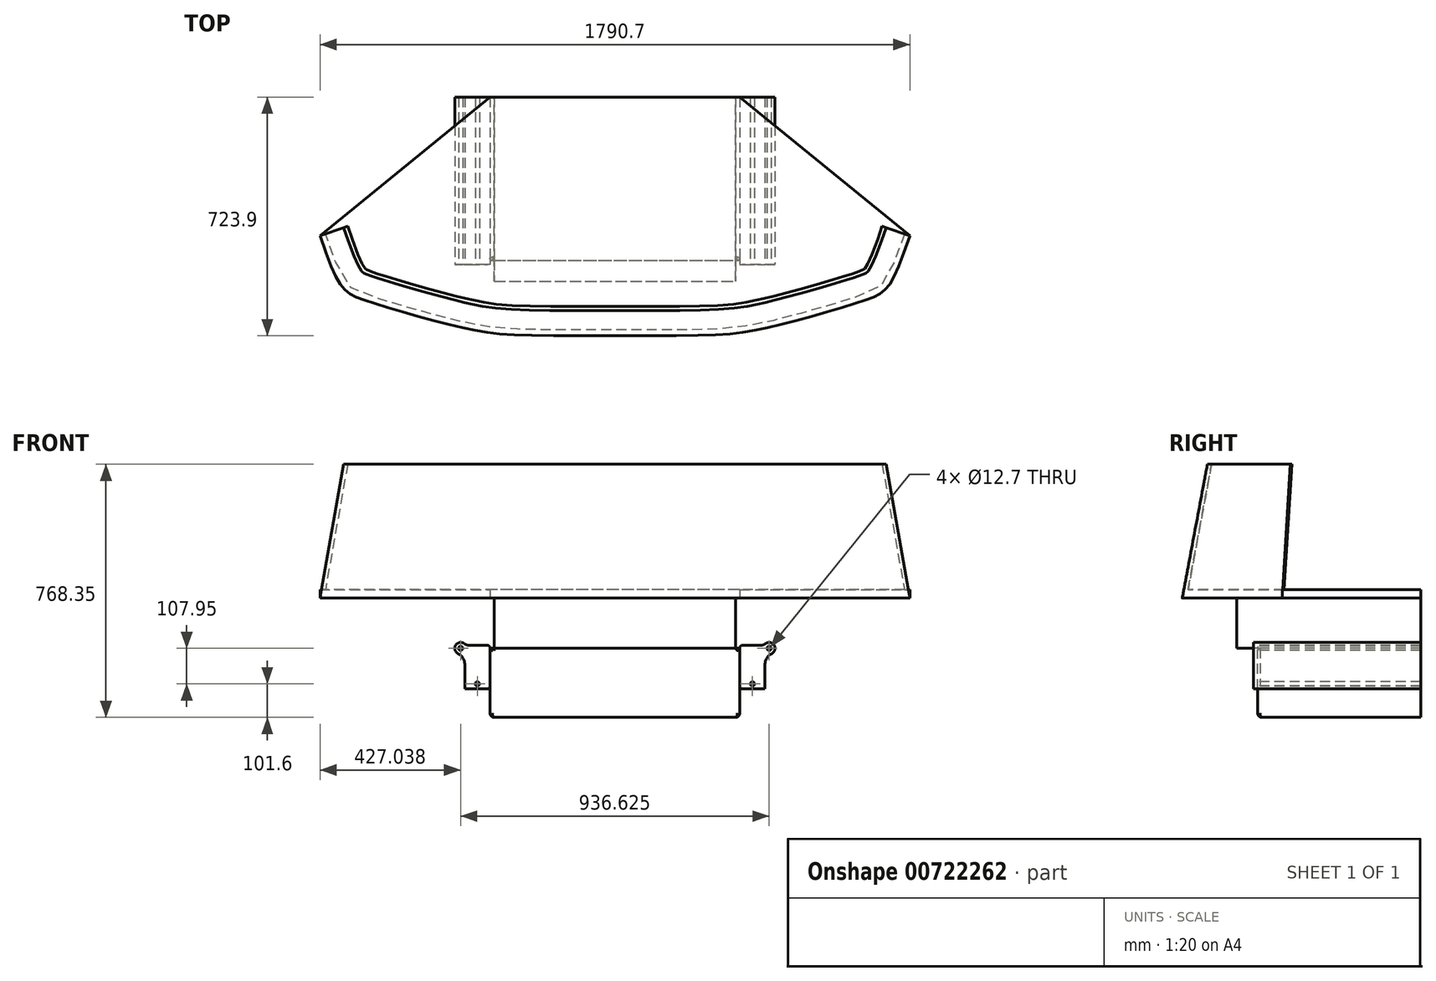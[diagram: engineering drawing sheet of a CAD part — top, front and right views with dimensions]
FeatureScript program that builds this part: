
annotation { "Feature Type Name" : "Feature", "Feature Type Description" : "" }
export const myFeature = defineFeature(function(context is Context, id is Id, definition is map)
    precondition{}
    {
        {
            var Q0;
            Q0=qCreatedBy(makeId("Front.planeOp"),FACE);
            var sketch = newSketch(context, id + "F0", { "sketchPlane" : qUnion([Q0])});
            skCircle(sketch, "E0", {"center": v(-468.31, 0) * mm, "radius": 6.35 * mm});
            skCircle(sketch, "E1", {"center": v(-417.51, -107.95) * mm, "radius": 6.35 * mm});
            skArc(sketch, "E2", {"start": v(-457.5, 14.12) * mm, "mid": v(-483.35, 9.48) * mm, "end": v(-476.4, -15.84) * mm});
            skLineSegment(sketch, "E3", {"start": v(-442.07, 8.9) * mm, "end": v(-379.41, 8.9) * mm});
            skLineSegment(sketch, "E4", {"start": v(-379.41, 8.89) * mm, "end": v(-379.41, -123.2) * mm});
            skLineSegment(sketch, "E5", {"start": v(-379.41, -123.2) * mm, "end": v(-455.61, -123.2) * mm});
            skLineSegment(sketch, "E6", {"start": v(-455.61, -123.2) * mm, "end": v(-455.61, -49.77) * mm});
            skPoint(sketch, "E7.visualSharp", {"position": v(-452.91, 8.9) * mm});
            skArc(sketch, "E7.filletArc", {"start": v(-457.5, 14.12) * mm, "mid": v(-450.22, 10.23) * mm, "end": v(-442.07, 8.89) * mm});
            skPoint(sketch, "E8.visualSharp", {"position": v(-455.61, -12.44) * mm});
            skArc(sketch, "E8.filletArc", {"start": v(-455.61, -49.77) * mm, "mid": v(-461.22, -29.88) * mm, "end": v(-476.4, -15.84) * mm});
            skLineSegment(sketch, "E9.MirrorCS", {"start": v(379.41, 8.89) * mm, "end": v(379.41, -123.2) * mm});
            skLineSegment(sketch, "E10.MirrorCS", {"start": v(442.07, 8.9) * mm, "end": v(379.41, 8.9) * mm});
            skArc(sketch, "E11.MirrorCS", {"start": v(457.5, 14.12) * mm, "mid": v(483.35, 9.48) * mm, "end": v(476.4, -15.84) * mm});
            skArc(sketch, "E12.MirrorCS", {"start": v(457.5, 14.12) * mm, "mid": v(450.22, 10.23) * mm, "end": v(442.07, 8.89) * mm});
            skArc(sketch, "E13.MirrorCS", {"start": v(455.61, -49.77) * mm, "mid": v(461.22, -29.88) * mm, "end": v(476.4, -15.84) * mm});
            skLineSegment(sketch, "E14.MirrorCS", {"start": v(455.61, -123.2) * mm, "end": v(455.61, -49.77) * mm});
            skLineSegment(sketch, "E15.MirrorCS", {"start": v(379.41, -123.2) * mm, "end": v(455.61, -123.2) * mm});
            skCircle(sketch, "E16.MirrorC", {"center": v(468.31, 0) * mm, "radius": 6.35 * mm});
            skCircle(sketch, "E17.MirrorC", {"center": v(417.51, -107.95) * mm, "radius": 6.35 * mm});
            skSolve(sketch);
        }
        {
            var Q0;
            Q0=makeQuery(id+"F0.imprint","IMPRINT",FACE,{"disambiguationData":[TD([[makeQuery(id+"F0.imprint","IMPRINT",EDGE,{"derivedFrom":sQuery(id+"F0.wireOp",EDGE,"E0")}),-1.0]])]});
            var Q1;
            Q1=makeQuery(id+"F0.imprint","IMPRINT",FACE,{"disambiguationData":[TD([[makeQuery(id+"F0.imprint","IMPRINT",EDGE,{"derivedFrom":sQuery(id+"F0.wireOp",EDGE,"E9.MirrorCS")}),1.0]])]});
            extrude(context, id + "F1", {"entities" : qUnion([Q0, Q1]), "oppositeDirection" : true, "depth" : 508 * mm, "offsetDistance" : 25.4 * mm});
        }
        {
            var Q0;
            Q0=makeQuery(id+"F1.opExtrude","CAP_FACE",FACE,{"disambiguationData":[OSD([sQuery(id+"F0.wireOp",EDGE,"E0"),sQuery(id+"F0.wireOp",EDGE,"E1"),sQuery(id+"F0.wireOp",EDGE,"E2"),sQuery(id+"F0.wireOp",EDGE,"E3"),sQuery(id+"F0.wireOp",EDGE,"E4"),sQuery(id+"F0.wireOp",EDGE,"E5"),sQuery(id+"F0.wireOp",EDGE,"E6"),sQuery(id+"F0.wireOp",EDGE,"E7.filletArc"),sQuery(id+"F0.wireOp",EDGE,"E8.filletArc")])],"isStart":true});
            cPlane(context, id + "F2", {"entities" : qUnion([Q0]), "cplaneType" : CPlaneType.OFFSET, "offset" : 50.8 * mm, "width" : 152.4 * mm, "height" : 152.4 * mm});
        }
        {
            var Q0;
            Q0=qCreatedBy(id+"F2.planeOp",FACE);
            var sketch = newSketch(context, id + "F3", { "sketchPlane" : qUnion([Q0])});
            skLineSegment(sketch, "E18.bottom", {"start": v(-366.71, 0) * mm, "end": v(366.71, 0) * mm});
            skLineSegment(sketch, "E18.top", {"start": v(-366.71, 177.8) * mm, "end": v(366.71, 177.8) * mm});
            skLineSegment(sketch, "E18.left", {"start": v(-366.71, 0) * mm, "end": v(-366.71, 177.8) * mm});
            skLineSegment(sketch, "E18.right", {"start": v(366.71, 0) * mm, "end": v(366.71, 177.8) * mm});
            skSolve(sketch);
        }
        {
            var Q0;
            Q0=makeQuery(id+"F3.imprint","IMPRINT",FACE,{"disambiguationData":[TD([[makeQuery(id+"F3.imprint","IMPRINT",EDGE,{"derivedFrom":sQuery(id+"F3.wireOp",EDGE,"E18.bottom")}),1.0]])]});
            var Q1;
            Q1=makeQuery(id+"F1.opExtrude","CAP_FACE",FACE,{"disambiguationData":[OSD([sQuery(id+"F0.wireOp",EDGE,"E0"),sQuery(id+"F0.wireOp",EDGE,"E1"),sQuery(id+"F0.wireOp",EDGE,"E2"),sQuery(id+"F0.wireOp",EDGE,"E3"),sQuery(id+"F0.wireOp",EDGE,"E4"),sQuery(id+"F0.wireOp",EDGE,"E5"),sQuery(id+"F0.wireOp",EDGE,"E6"),sQuery(id+"F0.wireOp",EDGE,"E7.filletArc"),sQuery(id+"F0.wireOp",EDGE,"E8.filletArc")])],"isStart":false});
            extrude(context, id + "F4", {"entities" : qUnion([Q0]), "endBound" : BoundingType.UP_TO_SURFACE, "oppositeDirection" : true, "depth" : 25.4 * mm, "endBoundEntityFace" : qUnion([Q1]), "offsetDistance" : 25.4 * mm});
        }
        {
            var Q0;
            Q0=makeQuery(id+"F1.opExtrude","CAP_FACE",FACE,{"disambiguationData":[OSD([sQuery(id+"F0.wireOp",EDGE,"E0"),sQuery(id+"F0.wireOp",EDGE,"E1"),sQuery(id+"F0.wireOp",EDGE,"E2"),sQuery(id+"F0.wireOp",EDGE,"E3"),sQuery(id+"F0.wireOp",EDGE,"E4"),sQuery(id+"F0.wireOp",EDGE,"E5"),sQuery(id+"F0.wireOp",EDGE,"E6"),sQuery(id+"F0.wireOp",EDGE,"E7.filletArc"),sQuery(id+"F0.wireOp",EDGE,"E8.filletArc")])],"isStart":true});
            cPlane(context, id + "F5", {"entities" : qUnion([Q0]), "cplaneType" : CPlaneType.OFFSET, "offset" : 12.7 * mm, "oppositeDirection" : true, "width" : 152.4 * mm, "height" : 152.4 * mm});
        }
        {
            var Q0;
            Q0=qCreatedBy(id+"F5.planeOp",FACE);
            var sketch = newSketch(context, id + "F6", { "sketchPlane" : qUnion([Q0])});
            skLineSegment(sketch, "E19.0.0", {"start": v(-455.61, -49.77) * mm, "end": v(-455.61, -123.2) * mm});
            skLineSegment(sketch, "E19.0.1", {"start": v(-455.61, -123.2) * mm, "end": v(-379.41, -123.2) * mm});
            skLineSegment(sketch, "E19.0.2", {"start": v(-379.41, -123.2) * mm, "end": v(-379.41, 8.89) * mm});
            skLineSegment(sketch, "E19.0.3", {"start": v(-379.41, 8.9) * mm, "end": v(-442.07, 8.9) * mm});
            skArc(sketch, "E19.0.4", {"start": v(-442.07, 8.89) * mm, "mid": v(-450.22, 10.23) * mm, "end": v(-457.5, 14.12) * mm});
            skArc(sketch, "E19.0.5", {"start": v(-457.5, 14.12) * mm, "mid": v(-483.35, 9.48) * mm, "end": v(-476.4, -15.84) * mm});
            skArc(sketch, "E19.0.6", {"start": v(-476.4, -15.84) * mm, "mid": v(-461.22, -29.88) * mm, "end": v(-455.61, -49.77) * mm});
            skLineSegment(sketch, "E20.0.0", {"start": v(366.71, 177.8) * mm, "end": v(-366.71, 177.8) * mm});
            skLineSegment(sketch, "E20.0.1", {"start": v(-366.71, 177.8) * mm, "end": v(-366.71, 0) * mm});
            skLineSegment(sketch, "E20.0.2", {"start": v(-366.71, 0) * mm, "end": v(366.71, 0) * mm});
            skLineSegment(sketch, "E20.0.3", {"start": v(366.71, 0) * mm, "end": v(366.71, 177.8) * mm});
            skLineSegment(sketch, "E21.0.0", {"start": v(379.41, -123.2) * mm, "end": v(455.61, -123.2) * mm});
            skLineSegment(sketch, "E21.0.1", {"start": v(455.61, -123.2) * mm, "end": v(455.61, -49.77) * mm});
            skArc(sketch, "E21.0.2", {"start": v(455.61, -49.77) * mm, "mid": v(461.22, -29.88) * mm, "end": v(476.4, -15.84) * mm});
            skArc(sketch, "E21.0.3", {"start": v(476.4, -15.84) * mm, "mid": v(483.35, 9.48) * mm, "end": v(457.5, 14.12) * mm});
            skArc(sketch, "E21.0.4", {"start": v(457.5, 14.12) * mm, "mid": v(450.22, 10.23) * mm, "end": v(442.07, 8.89) * mm});
            skLineSegment(sketch, "E21.0.5", {"start": v(442.07, 8.9) * mm, "end": v(379.41, 8.9) * mm});
            skLineSegment(sketch, "E21.0.6", {"start": v(379.41, 8.89) * mm, "end": v(379.41, -123.2) * mm});
            skLineSegment(sketch, "E22.bottom", {"start": v(-379.41, 0) * mm, "end": v(379.41, 0) * mm});
            skLineSegment(sketch, "E22.top", {"start": v(-379.41, -209.55) * mm, "end": v(379.41, -209.55) * mm});
            skLineSegment(sketch, "E22.left", {"start": v(-379.41, 0) * mm, "end": v(-379.41, -209.55) * mm});
            skLineSegment(sketch, "E22.right", {"start": v(379.41, 0) * mm, "end": v(379.41, -209.55) * mm});
            skSolve(sketch);
        }
        {
            var Q0;
            {var subQ0=sQuery(id+"F6.wireOp",EDGE,"E22.top");Q0=makeQuery(id+"F6.imprint","IMPRINT",FACE,{"disambiguationData":[TD([[makeQuery(id+"F6.imprint","IMPRINT",EDGE,{"derivedFrom":subQ0}),1.0]])]});}
            var Q1;
            Q1=makeQuery(id+"F1.opExtrude","CAP_FACE",FACE,{"disambiguationData":[OSD([sQuery(id+"F0.wireOp",EDGE,"E0"),sQuery(id+"F0.wireOp",EDGE,"E1"),sQuery(id+"F0.wireOp",EDGE,"E2"),sQuery(id+"F0.wireOp",EDGE,"E3"),sQuery(id+"F0.wireOp",EDGE,"E4"),sQuery(id+"F0.wireOp",EDGE,"E5"),sQuery(id+"F0.wireOp",EDGE,"E6"),sQuery(id+"F0.wireOp",EDGE,"E7.filletArc"),sQuery(id+"F0.wireOp",EDGE,"E8.filletArc")])],"isStart":false});
            extrude(context, id + "F7", {"entities" : qUnion([Q0]), "operationType" : NewBodyOperationType.ADD, "endBound" : BoundingType.UP_TO_SURFACE, "oppositeDirection" : true, "depth" : 25.4 * mm, "endBoundEntityFace" : qUnion([Q1]), "offsetDistance" : 25.4 * mm});
        }
        {
            var Q0;
            Q0=makeQuery(id+"F4.opExtrude","SWEPT_FACE",FACE,{"disambiguationData":[OSD([sQuery(id+"F3.wireOp",EDGE,"E18.bottom")])]});
            cPlane(context, id + "F8", {"entities" : qUnion([Q0]), "cplaneType" : CPlaneType.OFFSET, "offset" : 152.4 * mm, "oppositeDirection" : true, "width" : 152.4 * mm, "height" : 152.4 * mm});
        }
        {
            var Q0;
            Q0=qCreatedBy(id+"F8.planeOp",FACE);
            var sketch = newSketch(context, id + "F9", { "sketchPlane" : qUnion([Q0])});
            skLineSegment(sketch, "E23", {"start": v(0, -54.17) * mm, "end": v(0, 215.9) * mm, "construction": true});
            skLineSegment(sketch, "E24.0", {"start": v(-366.71, -508) * mm, "end": v(-366.71, 50.8) * mm});
            skPoint(sketch, "E25.0", {"position": v(-379.41, -12.7) * mm});
            skLineSegment(sketch, "E26.0", {"start": v(-474.66, 0) * mm, "end": v(-461.96, 0) * mm});
            skLineSegment(sketch, "E27", {"start": v(-468.31, 0) * mm, "end": v(-468.31, 190.5) * mm, "construction": true});
            skLineSegment(sketch, "E28", {"start": v(-379.41, -12.7) * mm, "end": v(-958.78, -12.7) * mm, "construction": true});
            skLineSegment(sketch, "E29", {"start": v(-819.15, -12.7) * mm, "end": v(-819.15, 77.47) * mm, "construction": true});
            skLineSegment(sketch, "E30", {"start": v(-895.35, -12.7) * mm, "end": v(-895.35, -87.63) * mm, "construction": true});
            skLineSegment(sketch, "E31", {"start": v(-760.92, -12.7) * mm, "end": v(-746.44, 112.74) * mm, "construction": true});
            skFitSpline(sketch, "E32", {"points": [v(-895.35, -87.63) * mm, v(-819.15, 77.47) * mm, v(-746.44, 112.74) * mm, v(-468.31, 190.5) * mm, v(0, 215.9) * mm], "startDerivative": vector(453.5, 1324.2) * mm, "endDerivative": vector(2625.94, 0) * mm});
            skLineSegment(sketch, "E33", {"start": v(0, 215.9) * mm, "end": v(158.44, 215.9) * mm, "construction": true});
            skFitSpline(sketch, "E34.MirrorCS", {"points": [v(895.35, -87.63) * mm, v(819.15, 77.47) * mm, v(746.44, 112.74) * mm, v(468.31, 190.5) * mm, v(0, 215.9) * mm], "startDerivative": vector(-453.5, 1324.2) * mm, "endDerivative": vector(-2625.94, 0) * mm});
            skFitSpline(sketch, "E35.0", {"points": [v(883.34, -91.74) * mm, v(873.9, -64.22) * mm, v(861.67, -29.48) * mm, v(847.7, 5.9) * mm, v(838.03, 27.49) * mm, v(830.4, 41.8) * mm, v(824.41, 51.31) * mm, v(819.95, 57.58) * mm, v(815.47, 63.07) * mm, v(811.67, 67.08) * mm, v(808.57, 70) * mm, v(805.4, 72.76) * mm, v(801.3, 75.93) * mm, v(795.98, 79.42) * mm, v(790.1, 82.7) * mm, v(783.56, 85.87) * mm, v(776.22, 88.98) * mm, v(768, 92.1) * mm, v(760.35, 94.79) * mm, v(753.71, 97.02) * mm, v(748.47, 98.74) * mm, v(742.95, 100.53) * mm, v(735.23, 103) * mm, v(724.92, 106.26) * mm, v(711.63, 110.38) * mm, v(697.5, 114.7) * mm, v(677.72, 120.67) * mm, v(651.43, 128.44) * mm, v(618.2, 138) * mm, v(584.12, 147.57) * mm, v(555.66, 155.3) * mm, v(533.28, 161.24) * mm, v(516.78, 165.52) * mm, v(500.67, 169.61) * mm, v(487.66, 172.83) * mm, v(477.55, 175.27) * mm, v(470.13, 177.04) * mm, v(462.89, 178.73) * mm, v(453.48, 180.88) * mm, v(442.1, 183.38) * mm, v(428.94, 186.1) * mm, v(416.07, 188.56) * mm, v(399.08, 191.5) * mm, v(377.73, 194.58) * mm, v(350.51, 197.46) * mm, v(320.32, 199.62) * mm, v(285.79, 201.17) * mm, v(245.6, 202.2) * mm, v(198.45, 202.8) * mm, v(124.53, 203.2) * mm, v(54.7, 203.2) * mm, v(0, 203.2) * mm]});
            skFitSpline(sketch, "E35.1", {"points": [v(-883.34, -91.74) * mm, v(-873.9, -64.22) * mm, v(-861.67, -29.48) * mm, v(-847.7, 5.9) * mm, v(-838.03, 27.49) * mm, v(-830.4, 41.8) * mm, v(-824.41, 51.31) * mm, v(-819.95, 57.58) * mm, v(-815.47, 63.07) * mm, v(-811.67, 67.08) * mm, v(-808.57, 70) * mm, v(-805.4, 72.76) * mm, v(-801.3, 75.93) * mm, v(-795.98, 79.42) * mm, v(-790.1, 82.7) * mm, v(-783.56, 85.87) * mm, v(-776.22, 88.98) * mm, v(-768, 92.1) * mm, v(-760.35, 94.79) * mm, v(-753.71, 97.02) * mm, v(-748.47, 98.74) * mm, v(-742.95, 100.53) * mm, v(-735.23, 103) * mm, v(-724.92, 106.26) * mm, v(-711.63, 110.38) * mm, v(-697.5, 114.7) * mm, v(-677.72, 120.67) * mm, v(-651.43, 128.44) * mm, v(-618.2, 138) * mm, v(-584.12, 147.57) * mm, v(-555.66, 155.3) * mm, v(-533.28, 161.24) * mm, v(-516.78, 165.52) * mm, v(-500.67, 169.61) * mm, v(-487.66, 172.83) * mm, v(-477.55, 175.27) * mm, v(-470.13, 177.04) * mm, v(-462.89, 178.73) * mm, v(-453.48, 180.88) * mm, v(-442.1, 183.38) * mm, v(-428.94, 186.1) * mm, v(-416.07, 188.56) * mm, v(-399.08, 191.5) * mm, v(-377.73, 194.58) * mm, v(-350.51, 197.46) * mm, v(-320.32, 199.62) * mm, v(-285.79, 201.17) * mm, v(-245.6, 202.2) * mm, v(-198.45, 202.8) * mm, v(-124.53, 203.2) * mm, v(-54.7, 203.2) * mm, v(0, 203.2) * mm]});
            skLineSegment(sketch, "E36", {"start": v(-895.35, -87.63) * mm, "end": v(-883.34, -91.74) * mm});
            skLineSegment(sketch, "E37", {"start": v(895.35, -87.63) * mm, "end": v(883.34, -91.74) * mm});
            skSolve(sketch);
        }
        {
            var Q0;
            Q0=makeQuery(id+"F4.opExtrude","SWEPT_FACE",FACE,{"disambiguationData":[OSD([sQuery(id+"F3.wireOp",EDGE,"E18.top")])]});
            cPlane(context, id + "F10", {"entities" : qUnion([Q0]), "cplaneType" : CPlaneType.OFFSET, "offset" : 381 * mm, "width" : 152.4 * mm, "height" : 152.4 * mm});
        }
        {
            var Q0;
            Q0=qCreatedBy(id+"F10.planeOp",FACE);
            var sketch = newSketch(context, id + "F11", { "sketchPlane" : qUnion([Q0])});
            skFitSpline(sketch, "E38.0", {"points": [v(-895.35, 87.63) * mm, v(-862, -9.75) * mm, v(-832.5, -82.24) * mm, v(-744.32, -115.56) * mm, v(-396.35, -216.19) * mm, v(-310.12, -215.9) * mm, v(0, -215.9) * mm]});
            skFitSpline(sketch, "E39.0", {"points": [v(895.35, 87.63) * mm, v(862, -9.75) * mm, v(832.5, -82.24) * mm, v(744.32, -115.56) * mm, v(396.35, -216.19) * mm, v(310.12, -215.9) * mm, v(0, -215.9) * mm]});
            skFitSpline(sketch, "E40.0", {"points": [v(823.26, 112.32) * mm, v(818.6, 98.7) * mm, v(809.95, 73.78) * mm, v(798.72, 42.96) * mm, v(790.64, 22.53) * mm, v(784.88, 9.22) * mm, v(780.92, 0.74) * mm, v(777.36, -6.27) * mm, v(774.2, -11.86) * mm, v(771.52, -16.1) * mm, v(769.7, -18.65) * mm, v(768.49, -20.18) * mm, v(767.7, -21.11) * mm, v(767.01, -21.87) * mm, v(766.51, -22.37) * mm, v(766.14, -22.73) * mm, v(765.8, -23.04) * mm, v(765.41, -23.38) * mm, v(764.95, -23.75) * mm, v(764.27, -24.26) * mm, v(763.16, -25) * mm, v(760.95, -26.25) * mm, v(757.54, -27.92) * mm, v(752.7, -29.98) * mm, v(746.33, -32.4) * mm, v(739.74, -34.72) * mm, v(733.7, -36.75) * mm, v(729.62, -38.1) * mm, v(726.16, -39.22) * mm, v(723.47, -40.09) * mm, v(720.69, -40.98) * mm, v(716.9, -42.2) * mm, v(711.99, -43.75) * mm, v(703.79, -46.33) * mm, v(692.94, -49.7) * mm, v(679.07, -53.94) * mm, v(664.45, -58.34) * mm, v(649.2, -62.88) * mm, v(628.18, -69.05) * mm, v(600.84, -76.93) * mm, v(567.2, -86.36) * mm, v(533.56, -95.52) * mm, v(506.23, -102.69) * mm, v(485.23, -108.02) * mm, v(472.55, -111.15) * mm, v(462.75, -113.52) * mm, v(455.57, -115.23) * mm, v(448.6, -116.86) * mm, v(441.83, -118.4) * mm, v(435.28, -119.86) * mm, v(426.77, -121.7) * mm, v(416.53, -123.82) * mm, v(404.68, -126.08) * mm, v(389.2, -128.76) * mm, v(369.9, -131.55) * mm, v(345.02, -134.19) * mm, v(316.77, -136.21) * mm, v(283.68, -137.7) * mm, v(244.47, -138.7) * mm, v(197.93, -139.3) * mm, v(142.83, -139.6) * mm, v(77.96, -139.7) * mm, v(27.36, -139.7) * mm, v(0, -139.7) * mm]});
            skFitSpline(sketch, "E40.1", {"points": [v(-823.26, 112.32) * mm, v(-818.6, 98.7) * mm, v(-809.95, 73.78) * mm, v(-798.72, 42.96) * mm, v(-790.64, 22.53) * mm, v(-784.88, 9.22) * mm, v(-780.92, 0.74) * mm, v(-777.36, -6.27) * mm, v(-774.2, -11.86) * mm, v(-771.52, -16.1) * mm, v(-769.7, -18.65) * mm, v(-768.49, -20.18) * mm, v(-767.7, -21.11) * mm, v(-767.01, -21.87) * mm, v(-766.51, -22.37) * mm, v(-766.14, -22.73) * mm, v(-765.8, -23.04) * mm, v(-765.41, -23.38) * mm, v(-764.95, -23.75) * mm, v(-764.27, -24.26) * mm, v(-763.16, -25) * mm, v(-760.95, -26.25) * mm, v(-757.54, -27.92) * mm, v(-752.7, -29.98) * mm, v(-746.33, -32.4) * mm, v(-739.74, -34.72) * mm, v(-733.7, -36.75) * mm, v(-729.62, -38.1) * mm, v(-726.16, -39.22) * mm, v(-723.47, -40.09) * mm, v(-720.69, -40.98) * mm, v(-716.9, -42.2) * mm, v(-711.99, -43.75) * mm, v(-703.79, -46.33) * mm, v(-692.94, -49.7) * mm, v(-679.07, -53.94) * mm, v(-664.45, -58.34) * mm, v(-649.2, -62.88) * mm, v(-628.18, -69.05) * mm, v(-600.84, -76.93) * mm, v(-567.2, -86.36) * mm, v(-533.56, -95.52) * mm, v(-506.23, -102.69) * mm, v(-485.23, -108.02) * mm, v(-472.55, -111.15) * mm, v(-462.75, -113.52) * mm, v(-455.57, -115.23) * mm, v(-448.6, -116.86) * mm, v(-441.83, -118.4) * mm, v(-435.28, -119.86) * mm, v(-426.77, -121.7) * mm, v(-416.53, -123.82) * mm, v(-404.68, -126.08) * mm, v(-389.2, -128.76) * mm, v(-369.9, -131.55) * mm, v(-345.02, -134.19) * mm, v(-316.77, -136.21) * mm, v(-283.68, -137.7) * mm, v(-244.47, -138.7) * mm, v(-197.93, -139.3) * mm, v(-142.83, -139.6) * mm, v(-77.96, -139.7) * mm, v(-27.36, -139.7) * mm, v(0, -139.7) * mm]});
            skFitSpline(sketch, "E41.0", {"points": [v(811.25, 116.43) * mm, v(806.6, 102.84) * mm, v(797.97, 78) * mm, v(786.83, 47.43) * mm, v(778.87, 27.33) * mm, v(773.28, 14.4) * mm, v(769.5, 6.28) * mm, v(766.14, -0.3) * mm, v(763.27, -5.4) * mm, v(760.94, -9.07) * mm, v(759.5, -11.07) * mm, v(758.64, -12.15) * mm, v(758.14, -12.74) * mm, v(757.77, -13.15) * mm, v(757.56, -13.36) * mm, v(757.43, -13.49) * mm, v(757.37, -13.55) * mm, v(757.33, -13.58) * mm, v(757.3, -13.6) * mm, v(757.28, -13.62) * mm, v(757.26, -13.64) * mm, v(757.24, -13.66) * mm, v(757.22, -13.67) * mm, v(757.2, -13.69) * mm, v(757.18, -13.7) * mm, v(757.16, -13.72) * mm, v(757.13, -13.74) * mm, v(757.1, -13.76) * mm, v(757.06, -13.8) * mm, v(757, -13.83) * mm, v(756.94, -13.87) * mm, v(756.84, -13.94) * mm, v(756.68, -14.05) * mm, v(756.45, -14.19) * mm, v(756.17, -14.36) * mm, v(755.7, -14.62) * mm, v(754.96, -15.02) * mm, v(753.73, -15.64) * mm, v(751.6, -16.63) * mm, v(747.99, -18.18) * mm, v(742, -20.47) * mm, v(735.62, -22.71) * mm, v(729.7, -24.7) * mm, v(725.67, -26.03) * mm, v(722.24, -27.14) * mm, v(719.58, -28) * mm, v(716.82, -28.89) * mm, v(713.05, -30.09) * mm, v(708.16, -31.64) * mm, v(700, -34.2) * mm, v(689.2, -37.56) * mm, v(675.38, -41.78) * mm, v(660.8, -46.18) * mm, v(645.6, -50.7) * mm, v(624.64, -56.86) * mm, v(597.37, -64.71) * mm, v(563.82, -74.12) * mm, v(530.28, -83.25) * mm, v(503.05, -90.4) * mm, v(482.14, -95.7) * mm, v(469.53, -98.82) * mm, v(459.78, -101.17) * mm, v(452.66, -102.87) * mm, v(445.73, -104.48) * mm, v(439.03, -106.01) * mm, v(432.54, -107.46) * mm, v(424.14, -109.28) * mm, v(414.05, -111.37) * mm, v(402.4, -113.59) * mm, v(387.23, -116.21) * mm, v(368.33, -118.94) * mm, v(343.93, -121.53) * mm, v(316.06, -123.53) * mm, v(283.26, -125) * mm, v(244.25, -126) * mm, v(197.82, -126.6) * mm, v(142.8, -126.9) * mm, v(77.96, -127) * mm, v(27.36, -127) * mm, v(0, -127) * mm]});
            skFitSpline(sketch, "E41.1", {"points": [v(-811.25, 116.43) * mm, v(-806.6, 102.84) * mm, v(-797.97, 78) * mm, v(-786.83, 47.43) * mm, v(-778.87, 27.33) * mm, v(-773.28, 14.4) * mm, v(-769.5, 6.28) * mm, v(-766.14, -0.3) * mm, v(-763.27, -5.4) * mm, v(-760.94, -9.07) * mm, v(-759.5, -11.07) * mm, v(-758.64, -12.15) * mm, v(-758.14, -12.74) * mm, v(-757.77, -13.15) * mm, v(-757.56, -13.36) * mm, v(-757.43, -13.49) * mm, v(-757.37, -13.55) * mm, v(-757.33, -13.58) * mm, v(-757.3, -13.6) * mm, v(-757.28, -13.62) * mm, v(-757.26, -13.64) * mm, v(-757.24, -13.66) * mm, v(-757.22, -13.67) * mm, v(-757.2, -13.69) * mm, v(-757.18, -13.7) * mm, v(-757.16, -13.72) * mm, v(-757.13, -13.74) * mm, v(-757.1, -13.76) * mm, v(-757.06, -13.8) * mm, v(-757, -13.83) * mm, v(-756.94, -13.87) * mm, v(-756.84, -13.94) * mm, v(-756.68, -14.05) * mm, v(-756.45, -14.19) * mm, v(-756.17, -14.36) * mm, v(-755.7, -14.62) * mm, v(-754.96, -15.02) * mm, v(-753.73, -15.64) * mm, v(-751.6, -16.63) * mm, v(-747.99, -18.18) * mm, v(-742, -20.47) * mm, v(-735.62, -22.71) * mm, v(-729.7, -24.7) * mm, v(-725.67, -26.03) * mm, v(-722.24, -27.14) * mm, v(-719.58, -28) * mm, v(-716.82, -28.89) * mm, v(-713.05, -30.09) * mm, v(-708.16, -31.64) * mm, v(-700, -34.2) * mm, v(-689.2, -37.56) * mm, v(-675.38, -41.78) * mm, v(-660.8, -46.18) * mm, v(-645.6, -50.7) * mm, v(-624.64, -56.86) * mm, v(-597.37, -64.71) * mm, v(-563.82, -74.12) * mm, v(-530.28, -83.25) * mm, v(-503.05, -90.4) * mm, v(-482.14, -95.7) * mm, v(-469.53, -98.82) * mm, v(-459.78, -101.17) * mm, v(-452.66, -102.87) * mm, v(-445.73, -104.48) * mm, v(-439.03, -106.01) * mm, v(-432.54, -107.46) * mm, v(-424.14, -109.28) * mm, v(-414.05, -111.37) * mm, v(-402.4, -113.59) * mm, v(-387.23, -116.21) * mm, v(-368.33, -118.94) * mm, v(-343.93, -121.53) * mm, v(-316.06, -123.53) * mm, v(-283.26, -125) * mm, v(-244.25, -126) * mm, v(-197.82, -126.6) * mm, v(-142.8, -126.9) * mm, v(-77.96, -127) * mm, v(-27.36, -127) * mm, v(0, -127) * mm]});
            skLineSegment(sketch, "E42", {"start": v(-823.26, 112.32) * mm, "end": v(-811.25, 116.43) * mm});
            skLineSegment(sketch, "E43", {"start": v(823.26, 112.32) * mm, "end": v(811.25, 116.43) * mm});
            skSolve(sketch);
        }
        {
            var Q0;
            Q0=makeQuery(id+"F11.imprint","IMPRINT",FACE,{"disambiguationData":[TD([[makeQuery(id+"F11.imprint","IMPRINT",EDGE,{"derivedFrom":sQuery(id+"F11.wireOp",EDGE,"E40.0")}),-1.0]])]});
            var Q1;
            Q1=makeQuery(id+"F9.imprint","IMPRINT",FACE,{"disambiguationData":[TD([[makeQuery(id+"F9.imprint","IMPRINT",EDGE,{"derivedFrom":sQuery(id+"F9.wireOp",EDGE,"E32")}),-1.0]])]});
            loft(context, id + "F12", {"sheetProfilesArray" : [{ "sheetProfileEntities" : qUnion([Q0]) }, { "sheetProfileEntities" : qUnion([Q1]) }]});
        }
        {
            var Q0;
            Q0=makeQuery(id+"F12.opLoft","CAP_FACE",FACE,{"disambiguationData":[OSD([makeQuery(id+"F9.imprint","IMPRINT",FACE,{"disambiguationData":[TD([[makeQuery(id+"F9.imprint","IMPRINT",EDGE,{"derivedFrom":sQuery(id+"F9.wireOp",EDGE,"E32")}),-1.0]])]})])],"isStart":true});
            var sketch = newSketch(context, id + "F13", { "sketchPlane" : qUnion([Q0])});
            skFitSpline(sketch, "E44.0", {"points": [v(0, 215.9) * mm, v(-19.56, 215.9) * mm, v(-32.73, 215.9) * mm, v(-39.53, 215.9) * mm, v(-53.62, 215.9) * mm, v(-65.83, 215.9) * mm, v(-76.17, 215.89) * mm, v(-88.64, 215.88) * mm, v(-99.94, 215.87) * mm, v(-110.1, 215.85) * mm, v(-121.4, 215.83) * mm, v(-131.85, 215.8) * mm, v(-141.46, 215.77) * mm, v(-151.8, 215.74) * mm, v(-161.45, 215.7) * mm, v(-170.43, 215.65) * mm, v(-179.9, 215.6) * mm, v(-188.83, 215.53) * mm, v(-197.18, 215.45) * mm, v(-205.89, 215.38) * mm, v(-214.12, 215.29) * mm, v(-221.87, 215.18) * mm, v(-229.88, 215.08) * mm, v(-237.48, 214.96) * mm, v(-244.68, 214.82) * mm, v(-252.05, 214.69) * mm, v(-259.08, 214.53) * mm, v(-265.76, 214.36) * mm, v(-272.56, 214.18) * mm, v(-279.07, 213.99) * mm, v(-285.28, 213.77) * mm, v(-291.58, 213.56) * mm, v(-297.62, 213.32) * mm, v(-303.41, 213.06) * mm, v(-309.26, 212.8) * mm, v(-314.9, 212.5) * mm, v(-320.32, 212.2) * mm, v(-325.78, 211.89) * mm, v(-331.06, 211.55) * mm, v(-336.17, 211.18) * mm, v(-341.29, 210.81) * mm, v(-346.28, 210.42) * mm, v(-351.13, 210) * mm, v(-355.97, 209.57) * mm, v(-360.71, 209.1) * mm, v(-365.36, 208.62) * mm, v(-369.98, 208.13) * mm, v(-374.54, 207.6) * mm, v(-379.03, 207.05) * mm, v(-383.48, 206.5) * mm, v(-387.91, 205.9) * mm, v(-392.31, 205.26) * mm, v(-396.65, 204.64) * mm, v(-401, 203.97) * mm, v(-405.37, 203.26) * mm, v(-409.65, 202.56) * mm, v(-413.98, 201.8) * mm, v(-418.36, 201.01) * mm, v(-422.64, 200.23) * mm, v(-427, 199.4) * mm, v(-431.46, 198.52) * mm, v(-435.78, 197.66) * mm, v(-440.24, 196.74) * mm, v(-444.84, 195.75) * mm, v(-449.25, 194.81) * mm, v(-453.86, 193.8) * mm, v(-458.65, 192.72) * mm, v(-463.23, 191.68) * mm, v(-468.03, 190.57) * mm, v(-473.07, 189.39) * mm, v(-477.94, 188.24) * mm, v(-482.97, 187.03) * mm, v(-488.16, 185.77) * mm, v(-498.22, 183.32) * mm, v(-508.84, 180.66) * mm, v(-520, 177.8) * mm, v(-530.7, 175.04) * mm, v(-541.83, 172.13) * mm, v(-553.38, 169.04) * mm, v(-564.46, 166.08) * mm, v(-575.83, 162.98) * mm, v(-587.5, 159.76) * mm, v(-598.7, 156.67) * mm, v(-610.06, 153.49) * mm, v(-621.53, 150.22) * mm, v(-632.63, 147.07) * mm, v(-643.69, 143.89) * mm, v(-654.7, 140.67) * mm, v(-665.43, 137.54) * mm, v(-675.93, 134.44) * mm, v(-686.2, 131.36) * mm, v(-696.29, 128.34) * mm, v(-705.96, 125.4) * mm, v(-715.23, 122.55) * mm, v(-724.4, 119.72) * mm, v(-732.99, 117.04) * mm, v(-740.97, 114.5) * mm, v(-742.96, 113.86) * mm, v(-744.9, 113.24) * mm, v(-746.8, 112.63) * mm, v(-748.8, 111.99) * mm, v(-750.65, 111.38) * mm, v(-752.37, 110.83) * mm, v(-754.24, 110.21) * mm, v(-756.01, 109.63) * mm, v(-757.68, 109.08) * mm, v(-759.45, 108.49) * mm, v(-761.14, 107.92) * mm, v(-762.74, 107.37) * mm, v(-766.17, 106.2) * mm, v(-769.32, 105.1) * mm, v(-772.19, 104.05) * mm, v(-775.28, 102.92) * mm, v(-778.14, 101.83) * mm, v(-780.8, 100.77) * mm, v(-783.59, 99.65) * mm, v(-786.2, 98.54) * mm, v(-788.65, 97.43) * mm, v(-791.19, 96.29) * mm, v(-793.59, 95.13) * mm, v(-795.84, 93.96) * mm, v(-798.16, 92.76) * mm, v(-800.37, 91.52) * mm, v(-802.46, 90.25) * mm, v(-804.6, 88.96) * mm, v(-806.64, 87.62) * mm, v(-808.6, 86.23) * mm, v(-810.58, 84.82) * mm, v(-812.5, 83.34) * mm, v(-814.34, 81.8) * mm, v(-816.2, 80.23) * mm, v(-818.02, 78.59) * mm, v(-819.78, 76.85) * mm, v(-821.56, 75.1) * mm, v(-823.3, 73.27) * mm, v(-825, 71.33) * mm, v(-826.71, 69.38) * mm, v(-828.4, 67.32) * mm, v(-830.05, 65.14) * mm, v(-831.71, 62.96) * mm, v(-833.35, 60.65) * mm, v(-834.98, 58.22) * mm, v(-836.6, 55.79) * mm, v(-838.22, 53.2) * mm, v(-839.84, 50.49) * mm, v(-841.44, 47.78) * mm, v(-843.05, 44.9) * mm, v(-844.67, 41.87) * mm, v(-846.28, 38.86) * mm, v(-847.9, 35.67) * mm, v(-849.53, 32.3) * mm, v(-851.15, 28.96) * mm, v(-852.8, 25.43) * mm, v(-854.47, 21.69) * mm, v(-856.12, 18) * mm, v(-857.81, 14.1) * mm, v(-859.54, 9.98) * mm, v(-861.24, 5.93) * mm, v(-862.98, 1.63) * mm, v(-864.78, -2.91) * mm, v(-866.54, -7.35) * mm, v(-868.36, -12.06) * mm, v(-870.25, -17.05) * mm, v(-872.08, -21.9) * mm, v(-874, -27.05) * mm, v(-876, -32.52) * mm, v(-877.9, -37.78) * mm, v(-879.93, -43.4) * mm, v(-882.05, -49.4) * mm, v(-884.07, -55.08) * mm, v(-886.22, -61.2) * mm, v(-888.5, -67.74) * mm, v(-890.61, -73.84) * mm, v(-892.9, -80.47) * mm, v(-895.35, -87.63) * mm]});
            skFitSpline(sketch, "E45.0", {"points": [v(895.35, -87.63) * mm, v(892.9, -80.47) * mm, v(890.61, -73.84) * mm, v(888.5, -67.74) * mm, v(886.22, -61.2) * mm, v(884.07, -55.08) * mm, v(882.05, -49.4) * mm, v(879.93, -43.4) * mm, v(877.9, -37.78) * mm, v(876, -32.52) * mm, v(874, -27.05) * mm, v(872.08, -21.9) * mm, v(870.25, -17.05) * mm, v(868.36, -12.06) * mm, v(866.54, -7.35) * mm, v(864.78, -2.91) * mm, v(862.98, 1.63) * mm, v(861.24, 5.93) * mm, v(859.54, 9.98) * mm, v(857.81, 14.1) * mm, v(856.12, 18) * mm, v(854.47, 21.69) * mm, v(852.8, 25.42) * mm, v(851.15, 28.96) * mm, v(849.53, 32.3) * mm, v(847.9, 35.67) * mm, v(846.28, 38.86) * mm, v(844.67, 41.87) * mm, v(843.05, 44.9) * mm, v(841.44, 47.77) * mm, v(839.84, 50.49) * mm, v(838.22, 53.2) * mm, v(836.6, 55.78) * mm, v(834.98, 58.22) * mm, v(833.35, 60.65) * mm, v(831.71, 62.96) * mm, v(830.05, 65.14) * mm, v(828.4, 67.32) * mm, v(826.71, 69.38) * mm, v(825, 71.33) * mm, v(823.3, 73.27) * mm, v(821.56, 75.1) * mm, v(819.78, 76.85) * mm, v(818.02, 78.59) * mm, v(816.2, 80.23) * mm, v(814.34, 81.8) * mm, v(812.5, 83.34) * mm, v(810.58, 84.82) * mm, v(808.6, 86.23) * mm, v(806.64, 87.62) * mm, v(804.6, 88.96) * mm, v(802.46, 90.25) * mm, v(800.37, 91.52) * mm, v(798.16, 92.75) * mm, v(795.84, 93.96) * mm, v(793.59, 95.13) * mm, v(791.19, 96.29) * mm, v(788.65, 97.43) * mm, v(786.2, 98.54) * mm, v(783.59, 99.65) * mm, v(780.8, 100.77) * mm, v(778.15, 101.83) * mm, v(775.28, 102.92) * mm, v(772.19, 104.05) * mm, v(769.32, 105.1) * mm, v(766.17, 106.2) * mm, v(762.74, 107.37) * mm, v(761.14, 107.92) * mm, v(759.45, 108.49) * mm, v(757.68, 109.08) * mm, v(756.02, 109.63) * mm, v(754.25, 110.21) * mm, v(752.37, 110.83) * mm, v(750.65, 111.38) * mm, v(748.8, 111.99) * mm, v(746.8, 112.63) * mm, v(744.9, 113.24) * mm, v(742.96, 113.86) * mm, v(740.97, 114.5) * mm, v(732.99, 117.04) * mm, v(724.4, 119.72) * mm, v(715.23, 122.55) * mm, v(705.96, 125.4) * mm, v(696.29, 128.34) * mm, v(686.2, 131.36) * mm, v(675.93, 134.44) * mm, v(665.43, 137.54) * mm, v(654.7, 140.67) * mm, v(643.69, 143.89) * mm, v(632.63, 147.07) * mm, v(621.53, 150.22) * mm, v(610.06, 153.49) * mm, v(598.7, 156.67) * mm, v(587.5, 159.76) * mm, v(575.84, 162.98) * mm, v(564.46, 166.08) * mm, v(553.38, 169.04) * mm, v(541.83, 172.13) * mm, v(530.7, 175.04) * mm, v(520, 177.8) * mm, v(508.84, 180.66) * mm, v(498.23, 183.32) * mm, v(488.16, 185.77) * mm, v(482.97, 187.03) * mm, v(477.94, 188.24) * mm, v(473.07, 189.39) * mm, v(468.03, 190.57) * mm, v(463.23, 191.68) * mm, v(458.65, 192.72) * mm, v(453.86, 193.8) * mm, v(449.25, 194.81) * mm, v(444.84, 195.75) * mm, v(440.24, 196.74) * mm, v(435.78, 197.66) * mm, v(431.46, 198.52) * mm, v(427, 199.4) * mm, v(422.64, 200.23) * mm, v(418.36, 201.01) * mm, v(413.98, 201.8) * mm, v(409.65, 202.56) * mm, v(405.37, 203.26) * mm, v(401, 203.97) * mm, v(396.65, 204.64) * mm, v(392.31, 205.26) * mm, v(387.91, 205.9) * mm, v(383.48, 206.5) * mm, v(379.03, 207.05) * mm, v(374.54, 207.6) * mm, v(369.98, 208.13) * mm, v(365.36, 208.62) * mm, v(360.71, 209.1) * mm, v(355.97, 209.57) * mm, v(351.13, 210) * mm, v(346.28, 210.42) * mm, v(341.3, 210.81) * mm, v(336.17, 211.18) * mm, v(331.06, 211.55) * mm, v(325.78, 211.89) * mm, v(320.32, 212.2) * mm, v(314.9, 212.5) * mm, v(309.26, 212.8) * mm, v(303.41, 213.06) * mm, v(297.62, 213.32) * mm, v(291.58, 213.56) * mm, v(285.28, 213.77) * mm, v(279.07, 213.99) * mm, v(272.57, 214.18) * mm, v(265.76, 214.36) * mm, v(259.08, 214.53) * mm, v(252.05, 214.69) * mm, v(244.68, 214.82) * mm, v(237.48, 214.96) * mm, v(229.88, 215.08) * mm, v(221.87, 215.18) * mm, v(214.12, 215.29) * mm, v(205.89, 215.38) * mm, v(197.18, 215.45) * mm, v(188.83, 215.53) * mm, v(179.91, 215.6) * mm, v(170.43, 215.65) * mm, v(161.45, 215.7) * mm, v(151.8, 215.74) * mm, v(141.46, 215.77) * mm, v(131.86, 215.8) * mm, v(121.4, 215.83) * mm, v(110.1, 215.85) * mm, v(99.94, 215.87) * mm, v(88.64, 215.88) * mm, v(76.17, 215.89) * mm, v(65.83, 215.9) * mm, v(53.62, 215.9) * mm, v(39.53, 215.9) * mm, v(32.73, 215.9) * mm, v(19.56, 215.9) * mm, v(0, 215.9) * mm]});
            skLineSegment(sketch, "E46.0.0", {"start": v(-379.41, -508) * mm, "end": v(379.41, -508) * mm});
            skLineSegment(sketch, "E46.0.1", {"start": v(379.41, -508) * mm, "end": v(379.41, -12.7) * mm});
            skLineSegment(sketch, "E46.0.2", {"start": v(379.41, -12.7) * mm, "end": v(-379.41, -12.7) * mm});
            skLineSegment(sketch, "E46.0.3", {"start": v(-379.41, -12.7) * mm, "end": v(-379.41, -508) * mm});
            skLineSegment(sketch, "E47", {"start": v(-895.35, -87.63) * mm, "end": v(-379.41, -508) * mm});
            skLineSegment(sketch, "E48", {"start": v(379.41, -508) * mm, "end": v(895.35, -87.63) * mm});
            skSolve(sketch);
        }
        {
            var Q0;
            Q0=makeQuery(id+"F13.imprint","IMPRINT",FACE,{"disambiguationData":[TD([[makeQuery(id+"F13.imprint","IMPRINT",EDGE,{"derivedFrom":sQuery(id+"F13.wireOp",EDGE,"E46.0.1")}),-1.0]])]});
            var Q1;
            Q1=makeQuery(id+"F13.imprint","IMPRINT",FACE,{"disambiguationData":[TD([[makeQuery(id+"F13.imprint","IMPRINT",EDGE,{"derivedFrom":sQuery(id+"F13.wireOp",EDGE,"E46.0.0")}),1.0]])]});
            extrude(context, id + "F14", {"entities" : qUnion([Q0, Q1]), "operationType" : NewBodyOperationType.ADD, "oppositeDirection" : true, "depth" : 25.4 * mm, "offsetDistance" : 25.4 * mm});
        }
        {
            var Q0;
            {var subQ0=sQuery(id+"F6.wireOp",EDGE,"E22.bottom");Q0=makeQuery(id+"F7.boolean.opBoolean","SPLIT",EDGE,{"disambiguationData":[topologyDisambiguationEdgeConnected([makeQuery(id+"F4.opExtrude","SWEPT_FACE",FACE,{"disambiguationData":[OSD([sQuery(id+"F3.wireOp",EDGE,"E18.bottom")])]}),makeQuery(id+"F7.opExtrude","CAP_FACE",FACE,{"disambiguationData":[OSD([subQ0,sQuery(id+"F6.wireOp",EDGE,"E22.top"),sQuery(id+"F6.wireOp",EDGE,"E22.left"),sQuery(id+"F6.wireOp",EDGE,"E22.right")])],"isStart":true})])],"derivedFrom":makeQuery(id+"F7.opExtrude","CAP_EDGE",EDGE,{"disambiguationData":[OSD([subQ0])],"isStart":true})});}
            var Q1;
            Q1=makeQuery(id+"F1.opExtrude","SWEPT_EDGE",EDGE,{"disambiguationData":[OSD([sQuery(id+"F0.wireOp",EDGE,"E9.MirrorCS"),sQuery(id+"F0.wireOp",EDGE,"E10.MirrorCS")])]});
            var Q2;
            {var subQ0=sQuery(id+"F6.wireOp",EDGE,"E22.right");Q2=makeQuery(id+"F7.boolean.opBoolean","SPLIT",EDGE,{"disambiguationData":[topologyDisambiguationEdgeConnected([makeQuery(id+"F1.opExtrude","SWEPT_FACE",FACE,{"disambiguationData":[OSD([sQuery(id+"F0.wireOp",EDGE,"E9.MirrorCS")])]})])],"derivedFrom":makeQuery(id+"F7.opExtrude","CAP_EDGE",EDGE,{"disambiguationData":[OSD([subQ0])],"isStart":true})});}
            var Q3;
            {var subQ0=sQuery(id+"F6.wireOp",EDGE,"E22.left");Q3=makeQuery(id+"F7.boolean.opBoolean","SPLIT",EDGE,{"disambiguationData":[topologyDisambiguationEdgeConnected([makeQuery(id+"F1.opExtrude","SWEPT_FACE",FACE,{"disambiguationData":[OSD([sQuery(id+"F0.wireOp",EDGE,"E4")])]})])],"derivedFrom":makeQuery(id+"F7.opExtrude","CAP_EDGE",EDGE,{"disambiguationData":[OSD([subQ0])],"isStart":true})});}
            var Q4;
            {var subQ0=sQuery(id+"F0.wireOp",EDGE,"E15.MirrorCS");Q4=makeQuery(id+"F7.boolean.opBoolean","SPLIT",EDGE,{"disambiguationData":[topologyDisambiguationEdgeConnected([makeQuery(id+"F7.opExtrude","SWEPT_FACE",FACE,{"disambiguationData":[OSD([sQuery(id+"F6.wireOp",EDGE,"E22.right")])]})])],"derivedFrom":makeQuery(id+"F1.opExtrude","SWEPT_EDGE",EDGE,{"disambiguationData":[OSD([sQuery(id+"F0.wireOp",EDGE,"E9.MirrorCS"),subQ0])]})});}
            var Q5;
            {var subQ0=sQuery(id+"F0.wireOp",EDGE,"E5");Q5=makeQuery(id+"F7.boolean.opBoolean","SPLIT",EDGE,{"disambiguationData":[topologyDisambiguationEdgeConnected([makeQuery(id+"F7.opExtrude","SWEPT_FACE",FACE,{"disambiguationData":[OSD([sQuery(id+"F6.wireOp",EDGE,"E22.left")])]})])],"derivedFrom":makeQuery(id+"F1.opExtrude","SWEPT_EDGE",EDGE,{"disambiguationData":[OSD([sQuery(id+"F0.wireOp",EDGE,"E4"),subQ0])]})});}
            var Q6;
            Q6=makeQuery(id+"F1.opExtrude","SWEPT_EDGE",EDGE,{"disambiguationData":[OSD([sQuery(id+"F0.wireOp",EDGE,"E3"),sQuery(id+"F0.wireOp",EDGE,"E4")])]});
            fillet(context, id + "F15", {"entities" : qUnion([Q0, Q1, Q2, Q3, Q4, Q5, Q6]), "radius" : 7.62 * mm, "tangentPropagation" : true, "allowEdgeOverflow" : false});
        }
        {
            var Q0;
            {var subQ0=sQuery(id+"F3.wireOp",EDGE,"E18.right");Q0=makeQuery(id+"F7.boolean.opBoolean","SPLIT",EDGE,{"disambiguationData":[topologyDisambiguationEdgeConnected([makeQuery(id+"F7.opExtrude","SWEPT_FACE",FACE,{"disambiguationData":[OSD([sQuery(id+"F6.wireOp",EDGE,"E22.bottom")])]})])],"derivedFrom":makeQuery(id+"F4.opExtrude","SWEPT_EDGE",EDGE,{"disambiguationData":[OSD([sQuery(id+"F3.wireOp",EDGE,"E18.bottom"),subQ0])]})});}
            var Q1;
            {var subQ0=sQuery(id+"F3.wireOp",EDGE,"E18.left");Q1=makeQuery(id+"F7.boolean.opBoolean","SPLIT",EDGE,{"disambiguationData":[topologyDisambiguationEdgeConnected([makeQuery(id+"F7.opExtrude","SWEPT_FACE",FACE,{"disambiguationData":[OSD([sQuery(id+"F6.wireOp",EDGE,"E22.bottom")])]})])],"derivedFrom":makeQuery(id+"F4.opExtrude","SWEPT_EDGE",EDGE,{"disambiguationData":[OSD([sQuery(id+"F3.wireOp",EDGE,"E18.bottom"),subQ0])]})});}
            fillet(context, id + "F16", {"entities" : qUnion([Q0, Q1]), "radius" : 5.08 * mm, "tangentPropagation" : true, "allowEdgeOverflow" : false});
        }
        {
            var Q0;
            Q0=makeQuery(id+"F7.opExtrude","CAP_EDGE",EDGE,{"disambiguationData":[OSD([sQuery(id+"F6.wireOp",EDGE,"E22.top")])],"isStart":true});
            fillet(context, id + "F17", {"entities" : qUnion([Q0]), "radius" : 12.7 * mm, "tangentPropagation" : true, "allowEdgeOverflow" : false});
        }
    });
